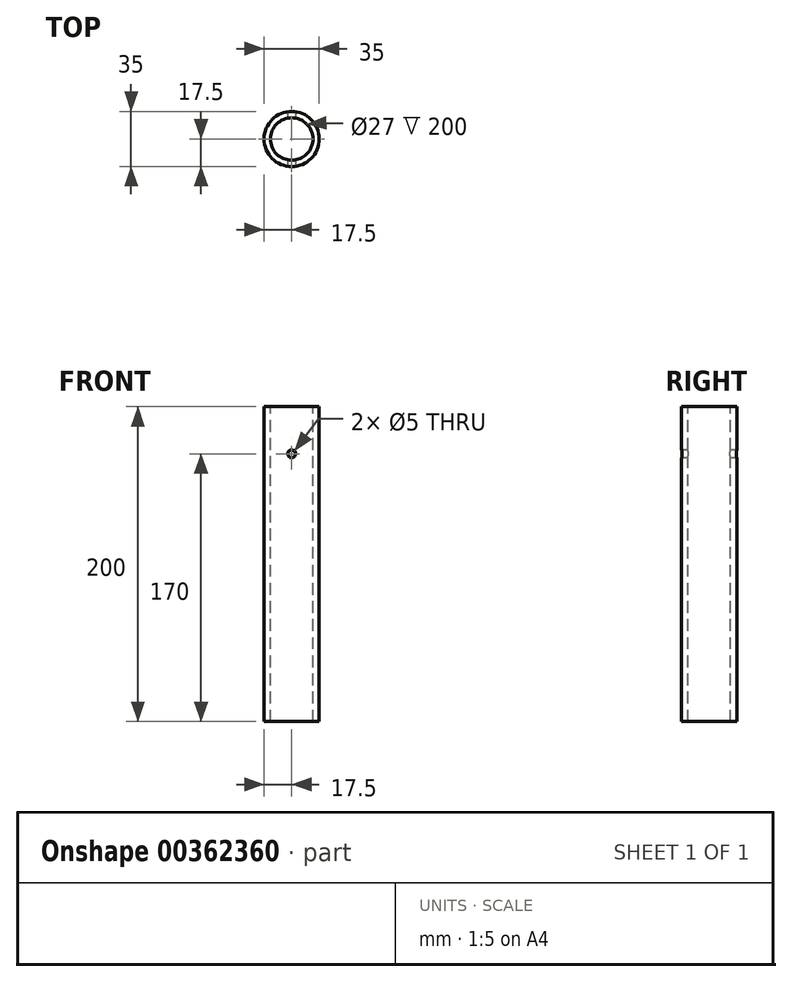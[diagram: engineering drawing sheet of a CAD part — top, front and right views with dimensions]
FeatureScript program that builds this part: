
annotation { "Feature Type Name" : "Feature", "Feature Type Description" : "" }
export const myFeature = defineFeature(function(context is Context, id is Id, definition is map)
    precondition{}
    {
        {
            var Q0;
            Q0=qCreatedBy(makeId("Top.planeOp"),FACE);
            var sketch = newSketch(context, id + "F0", { "sketchPlane" : qUnion([Q0])});
            skCircle(sketch, "E0", {"center": v(0, 0) * mm, "radius": 17.5 * mm});
            skSolve(sketch);
        }
        {
            var Q0;
            Q0=makeQuery(id+"F0.imprint","IMPRINT",FACE,{"disambiguationData":[TD([[makeQuery(id+"F0.imprint","IMPRINT",EDGE,{"derivedFrom":sQuery(id+"F0.wireOp",EDGE,"E0")}),1.0]])]});
            extrude(context, id + "F1", {"entities" : qUnion([Q0]), "depth" : 200 * mm});
        }
        {
            var Q0;
            Q0=qCreatedBy(makeId("Front.planeOp"),FACE);
            var sketch = newSketch(context, id + "F2", { "sketchPlane" : qUnion([Q0])});
            skCircle(sketch, "E1", {"center": v(0, 170) * mm, "radius": 2.5 * mm});
            skSolve(sketch);
        }
        {
            var Q0;
            Q0 = qSketchRegion(id + "F2", true);
            extrude(context, id + "F3", {"entities" : qUnion([Q0]), "operationType" : NewBodyOperationType.REMOVE, "oppositeDirection" : true, "depth" : 25 * mm, "hasSecondDirection" : true, "secondDirectionOppositeDirection" : false, "secondDirectionDepth" : 25 * mm});
        }
        {
            var Q0;
            Q0=makeQuery(id+"F1.opExtrude","CAP_FACE",FACE,{"disambiguationData":[OSD([sQuery(id+"F0.wireOp",EDGE,"E0")])],"isStart":false});
            var sketch = newSketch(context, id + "F4", { "sketchPlane" : qUnion([Q0])});
            skCircle(sketch, "E2", {"center": v(0, 0) * mm, "radius": 13.5 * mm});
            skSolve(sketch);
        }
        {
            var Q0;
            Q0 = qSketchRegion(id + "F4", true);
            extrude(context, id + "F5", {"entities" : qUnion([Q0]), "operationType" : NewBodyOperationType.REMOVE, "oppositeDirection" : true, "depth" : 1022 * mm});
        }
    });
